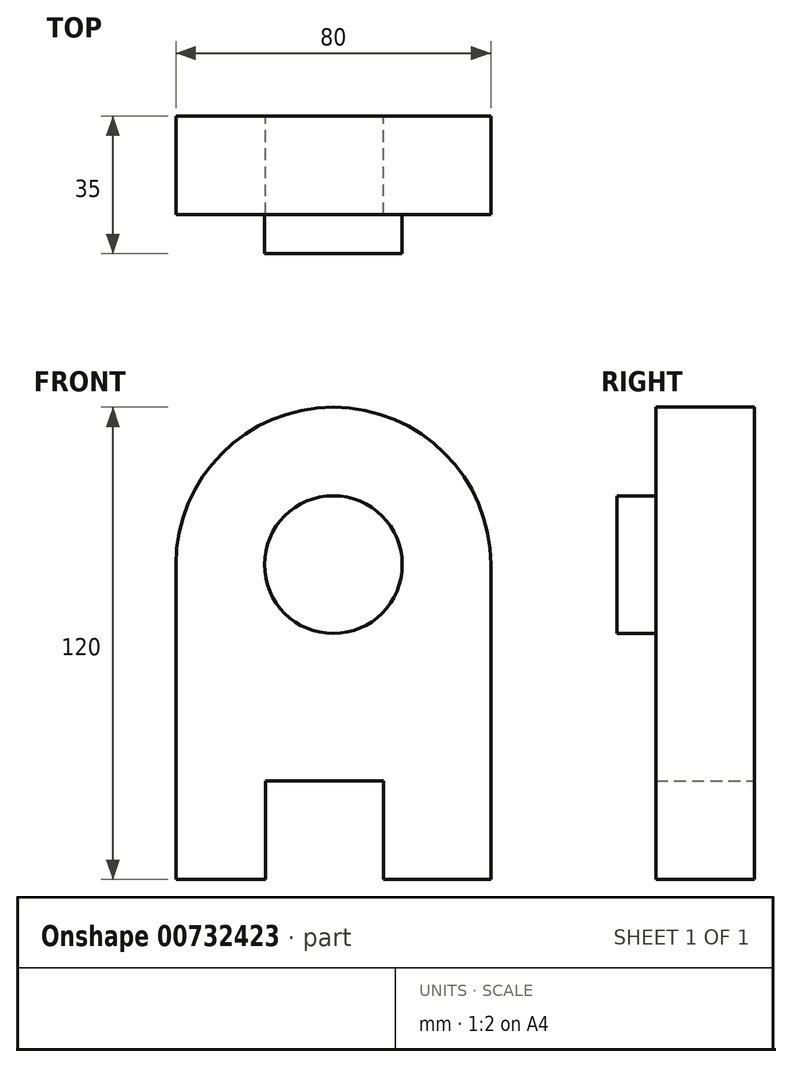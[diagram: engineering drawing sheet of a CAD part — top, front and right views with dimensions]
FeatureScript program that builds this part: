
annotation { "Feature Type Name" : "Feature", "Feature Type Description" : "" }
export const myFeature = defineFeature(function(context is Context, id is Id, definition is map)
    precondition{}
    {
        {
            var Q0;
            Q0=qCreatedBy(makeId("Front.planeOp"),FACE);
            var sketch = newSketch(context, id + "F0", { "sketchPlane" : qUnion([Q0])});
            skLineSegment(sketch, "E0", {"start": v(-40, 19.2) * mm, "end": v(-40, -5.8) * mm});
            skLineSegment(sketch, "E1", {"start": v(-40, -5.8) * mm, "end": v(-17.28, -5.8) * mm});
            skLineSegment(sketch, "E2", {"start": v(-17.28, -5.8) * mm, "end": v(-17.28, 19.2) * mm});
            skLineSegment(sketch, "E3", {"start": v(12.72, 19.2) * mm, "end": v(12.72, -5.8) * mm});
            skLineSegment(sketch, "E4", {"start": v(12.72, -5.8) * mm, "end": v(40, -5.8) * mm});
            skLineSegment(sketch, "E5", {"start": v(-17.28, 19.2) * mm, "end": v(12.72, 19.2) * mm});
            skLineSegment(sketch, "E6", {"start": v(40, -5.8) * mm, "end": v(40, 19.2) * mm});
            skCircle(sketch, "E7", {"center": v(0, 74.2) * mm, "radius": 17.5 * mm});
            skLineSegment(sketch, "E8", {"start": v(-40, 19.2) * mm, "end": v(-40, 74.2) * mm});
            skLineSegment(sketch, "E9", {"start": v(40, 74.2) * mm, "end": v(40, 19.2) * mm});
            skArc(sketch, "E10", {"start": v(40, 74.2) * mm, "mid": v(0, 114.2) * mm, "end": v(-40, 74.2) * mm});
            skSolve(sketch);
        }
        {
            var Q0;
            Q0=makeQuery(id+"F0.imprint","IMPRINT",FACE,{"disambiguationData":[TD([[makeQuery(id+"F0.imprint","IMPRINT",EDGE,{"derivedFrom":sQuery(id+"F0.wireOp",EDGE,"E7")}),1.0]])]});
            extrude(context, id + "F1", {"entities" : qUnion([Q0]), "depth" : 35 * mm, "offsetDistance" : 25 * mm});
        }
        {
            var Q0;
            Q0 = qSketchRegion(id + "F0", true);
            extrude(context, id + "F2", {"entities" : qUnion([Q0]), "operationType" : NewBodyOperationType.ADD, "depth" : 25 * mm, "offsetDistance" : 25 * mm});
        }
    });
